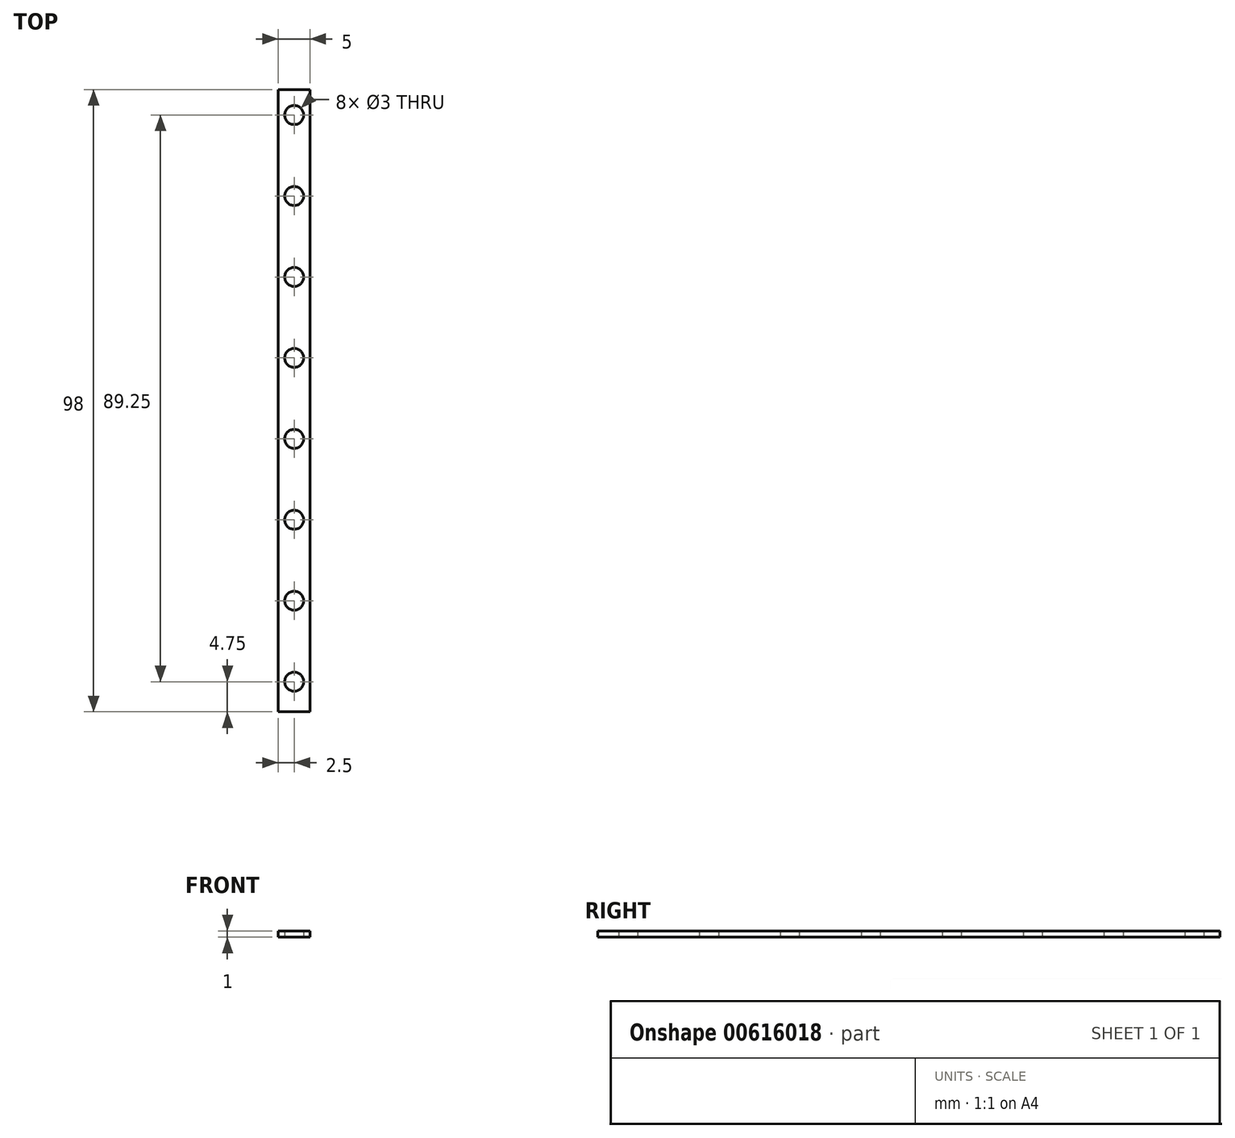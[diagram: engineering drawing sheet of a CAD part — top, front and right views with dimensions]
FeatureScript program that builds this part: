
annotation { "Feature Type Name" : "Feature", "Feature Type Description" : "" }
export const myFeature = defineFeature(function(context is Context, id is Id, definition is map)
    precondition{}
    {
        {
            var Q0;
            Q0=qCreatedBy(makeId("Top.planeOp"),FACE);
            var sketch = newSketch(context, id + "F0", { "sketchPlane" : qUnion([Q0])});
            skLineSegment(sketch, "E0.bottom", {"start": v(2.5, -49) * mm, "end": v(-2.5, -49) * mm});
            skLineSegment(sketch, "E0.top", {"start": v(2.5, 49) * mm, "end": v(-2.5, 49) * mm});
            skLineSegment(sketch, "E0.left", {"start": v(2.5, -49) * mm, "end": v(2.5, 49) * mm});
            skLineSegment(sketch, "E0.right", {"start": v(-2.5, -49) * mm, "end": v(-2.5, 49) * mm});
            skPoint(sketch, "E0.middle", {"position": v(0, 0) * mm});
            skCircle(sketch, "E1", {"center": v(0, 45) * mm, "radius": 1.5 * mm});
            skCircle(sketch, "E2.0.1.0", {"center": v(0, 32.25) * mm, "radius": 1.5 * mm});
            skCircle(sketch, "E2.0.2.0", {"center": v(0, 19.5) * mm, "radius": 1.5 * mm});
            skCircle(sketch, "E2.0.3.0", {"center": v(0, 6.75) * mm, "radius": 1.5 * mm});
            skCircle(sketch, "E2.0.4.0", {"center": v(0, -6) * mm, "radius": 1.5 * mm});
            skCircle(sketch, "E2.0.5.0", {"center": v(0, -18.75) * mm, "radius": 1.5 * mm});
            skCircle(sketch, "E2.0.6.0", {"center": v(0, -31.5) * mm, "radius": 1.5 * mm});
            skCircle(sketch, "E2.0.7.0", {"center": v(0, -44.25) * mm, "radius": 1.5 * mm});
            skLineSegment(sketch, "E2.direction1", {"start": v(0, 45) * mm, "end": v(25, 45) * mm, "construction": true});
            skLineSegment(sketch, "E2.direction2", {"start": v(0, 45) * mm, "end": v(0, 32.25) * mm, "construction": true});
            skSolve(sketch);
        }
        {
            var Q0;
            Q0=makeQuery(id+"F0.imprint","IMPRINT",FACE,{"disambiguationData":[TD([[makeQuery(id+"F0.imprint","IMPRINT",EDGE,{"derivedFrom":sQuery(id+"F0.wireOp",EDGE,"E0.bottom")}),-1.0]])]});
            extrude(context, id + "F1", {"entities" : qUnion([Q0]), "depth" : 1 * mm, "offsetDistance" : 25 * mm});
        }
    });
